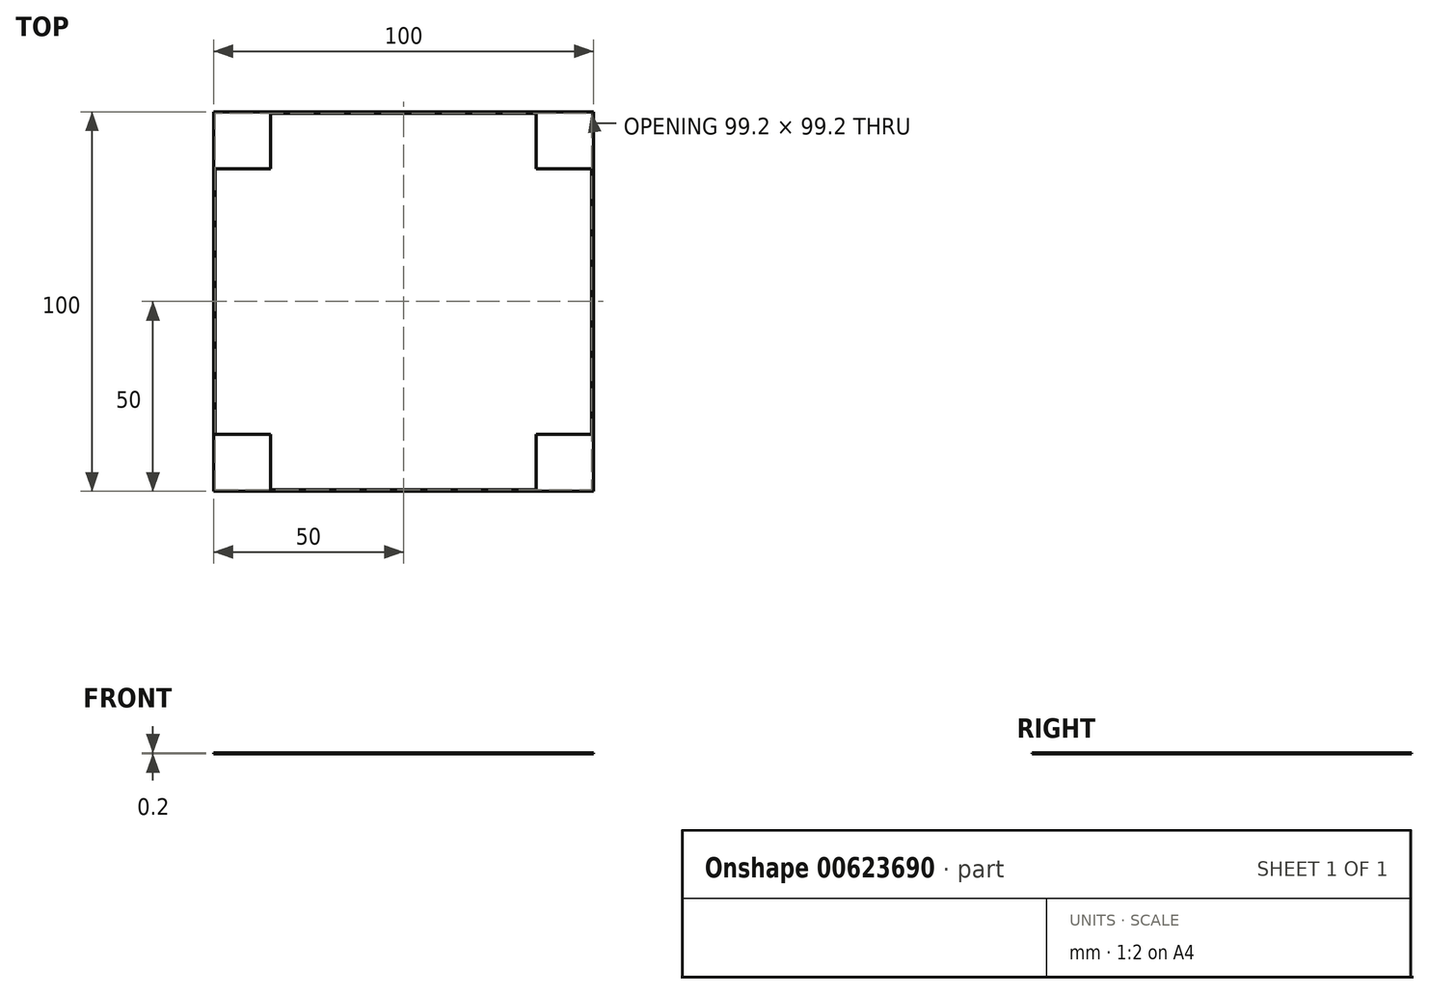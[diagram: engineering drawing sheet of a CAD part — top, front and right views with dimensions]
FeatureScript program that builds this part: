
annotation { "Feature Type Name" : "Feature", "Feature Type Description" : "" }
export const myFeature = defineFeature(function(context is Context, id is Id, definition is map)
    precondition{}
    {
        {
            var Q0;
            Q0=qCreatedBy(makeId("Top.planeOp"),FACE);
            var sketch = newSketch(context, id + "F0", { "sketchPlane" : qUnion([Q0])});
            skLineSegment(sketch, "E0.bottom", {"start": v(-50, 50) * mm, "end": v(-35, 50) * mm});
            skLineSegment(sketch, "E0.top", {"start": v(-50, 35) * mm, "end": v(-35, 35) * mm});
            skLineSegment(sketch, "E0.left", {"start": v(-50, 50) * mm, "end": v(-50, 35) * mm});
            skLineSegment(sketch, "E0.right", {"start": v(-35, 50) * mm, "end": v(-35, 35) * mm});
            skLineSegment(sketch, "E1.bottom", {"start": v(35, 50) * mm, "end": v(50, 50) * mm});
            skLineSegment(sketch, "E1.top", {"start": v(35, 35) * mm, "end": v(50, 35) * mm});
            skLineSegment(sketch, "E1.left", {"start": v(35, 50) * mm, "end": v(35, 35) * mm});
            skLineSegment(sketch, "E1.right", {"start": v(50, 50) * mm, "end": v(50, 35) * mm});
            skLineSegment(sketch, "E2.bottom", {"start": v(35, -35) * mm, "end": v(50, -35) * mm});
            skLineSegment(sketch, "E2.top", {"start": v(35, -50) * mm, "end": v(50, -50) * mm});
            skLineSegment(sketch, "E2.left", {"start": v(35, -35) * mm, "end": v(35, -50) * mm});
            skLineSegment(sketch, "E2.right", {"start": v(50, -35) * mm, "end": v(50, -50) * mm});
            skLineSegment(sketch, "E3.bottom", {"start": v(-50, -35) * mm, "end": v(-35, -35) * mm});
            skLineSegment(sketch, "E3.top", {"start": v(-50, -50) * mm, "end": v(-35, -50) * mm});
            skLineSegment(sketch, "E3.left", {"start": v(-50, -35) * mm, "end": v(-50, -50) * mm});
            skLineSegment(sketch, "E3.right", {"start": v(-35, -35) * mm, "end": v(-35, -50) * mm});
            skSolve(sketch);
        }
        {
            var Q0;
            Q0 = qSketchRegion(id + "F0", true);
            extrude(context, id + "F1", {"entities" : qUnion([Q0]), "depth" : .2 * mm, "offsetDistance" : 25 * mm});
        }
        {
            var Q0;
            Q0=qCreatedBy(makeId("Top.planeOp"),FACE);
            var sketch = newSketch(context, id + "F2", { "sketchPlane" : qUnion([Q0])});
            skLineSegment(sketch, "E4.bottom", {"start": v(-50, 50) * mm, "end": v(50, 50) * mm});
            skLineSegment(sketch, "E4.top", {"start": v(-50, -50) * mm, "end": v(50, -50) * mm});
            skLineSegment(sketch, "E4.left", {"start": v(-50, 50) * mm, "end": v(-50, -50) * mm});
            skLineSegment(sketch, "E4.right", {"start": v(50, 50) * mm, "end": v(50, -50) * mm});
            skLineSegment(sketch, "E5.bottom", {"start": v(49.6, 49.6) * mm, "end": v(-49.6, 49.6) * mm});
            skLineSegment(sketch, "E5.top", {"start": v(49.6, -49.6) * mm, "end": v(-49.6, -49.6) * mm});
            skLineSegment(sketch, "E5.left", {"start": v(49.6, 49.6) * mm, "end": v(49.6, -49.6) * mm});
            skLineSegment(sketch, "E5.right", {"start": v(-49.6, 49.6) * mm, "end": v(-49.6, -49.6) * mm});
            skPoint(sketch, "E5.middle", {"position": v(0, 0) * mm});
            skSolve(sketch);
        }
        {
            var Q0;
            Q0 = qSketchRegion(id + "F2", true);
            extrude(context, id + "F3", {"entities" : qUnion([Q0]), "operationType" : NewBodyOperationType.ADD, "depth" : .2 * mm, "offsetDistance" : 25 * mm});
        }
    });
